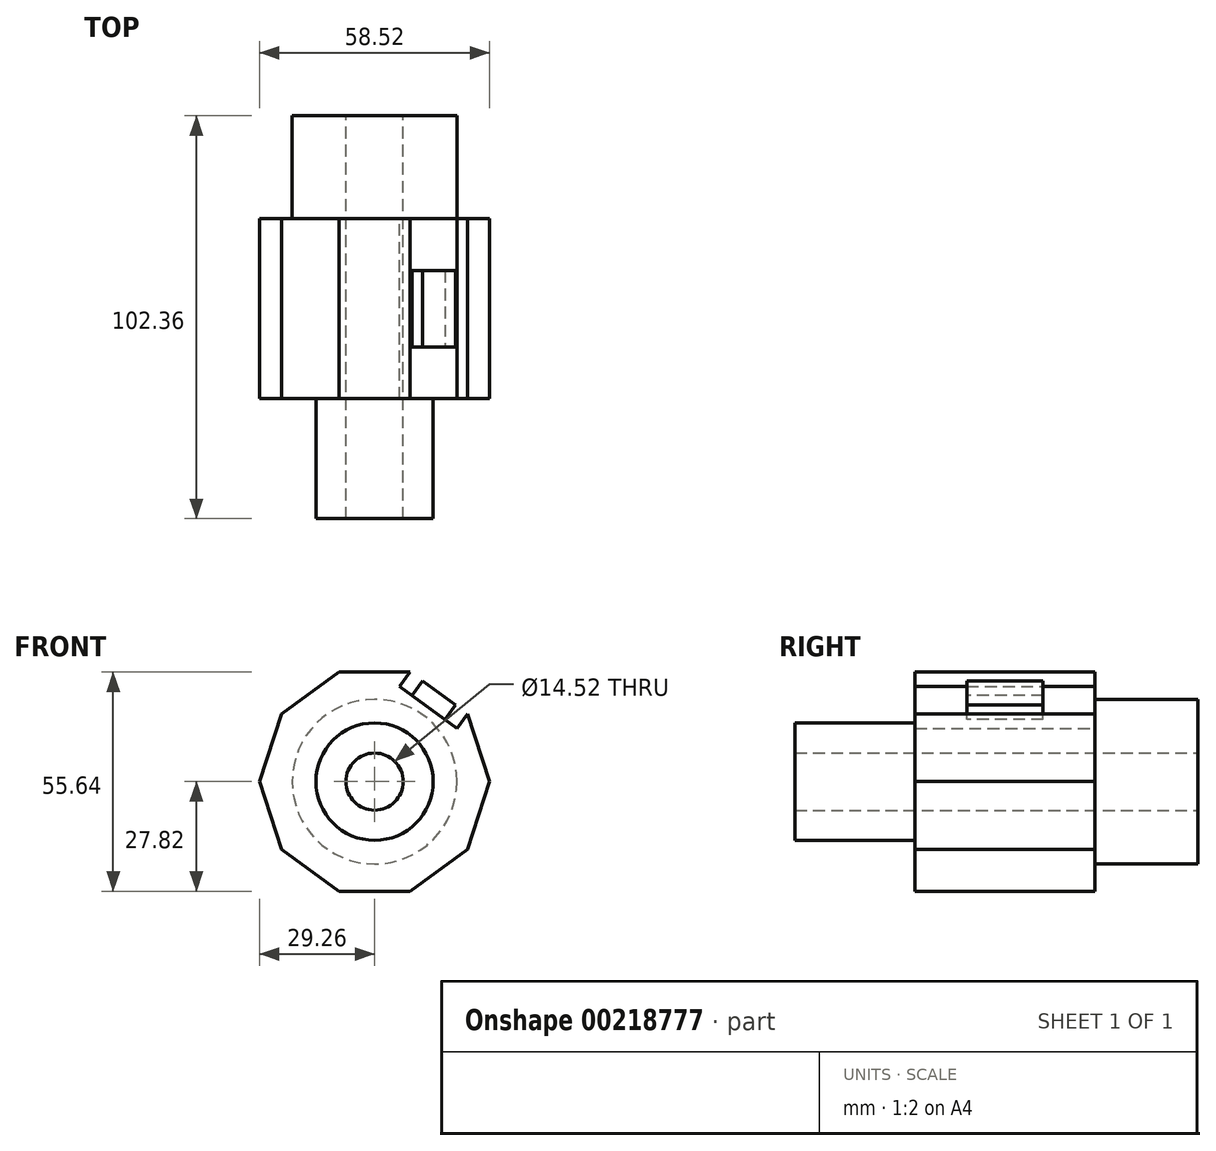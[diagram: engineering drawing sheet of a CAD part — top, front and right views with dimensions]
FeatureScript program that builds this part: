
annotation { "Feature Type Name" : "Feature", "Feature Type Description" : "" }
export const myFeature = defineFeature(function(context is Context, id is Id, definition is map)
    precondition{}
    {
        {
            var Q0;
            Q0=qCreatedBy(makeId("Front.planeOp"),FACE);
            var sketch = newSketch(context, id + "F0", { "sketchPlane" : qUnion([Q0])});
            skCircle(sketch, "E0.cCircle", {"center": v(0, 0) * mm, "radius": 27.82 * mm, "construction": true});
            skLineSegment(sketch, "E0.0", {"start": v(-9.04, 27.82) * mm, "end": v(9.04, 27.82) * mm});
            skLineSegment(sketch, "E0.1", {"start": v(9.04, 27.82) * mm, "end": v(23.67, 17.2) * mm});
            skLineSegment(sketch, "E0.2", {"start": v(23.67, 17.2) * mm, "end": v(29.26, 0) * mm});
            skLineSegment(sketch, "E0.3", {"start": v(29.26, 0) * mm, "end": v(23.67, -17.2) * mm});
            skLineSegment(sketch, "E0.4", {"start": v(23.67, -17.2) * mm, "end": v(9.04, -27.82) * mm});
            skLineSegment(sketch, "E0.5", {"start": v(9.04, -27.82) * mm, "end": v(-9.04, -27.82) * mm});
            skLineSegment(sketch, "E0.6", {"start": v(-9.04, -27.82) * mm, "end": v(-23.67, -17.2) * mm});
            skLineSegment(sketch, "E0.7", {"start": v(-23.67, -17.2) * mm, "end": v(-29.26, 0) * mm});
            skLineSegment(sketch, "E0.8", {"start": v(-29.26, 0) * mm, "end": v(-23.67, 17.2) * mm});
            skLineSegment(sketch, "E0.9", {"start": v(-23.67, 17.2) * mm, "end": v(-9.04, 27.82) * mm});
            skPoint(sketch, "E0.0.midPoint", {"position": v(0, 27.82) * mm});
            skSolve(sketch);
        }
        {
            var Q0;
            Q0=makeQuery(id+"F0.imprint","IMPRINT",FACE,{"disambiguationData":[TD([[makeQuery(id+"F0.imprint","IMPRINT",EDGE,{"derivedFrom":sQuery(id+"F0.wireOp",EDGE,"E0.0")}),-1.0]])]});
            extrude(context, id + "F1", {"entities" : qUnion([Q0]), "depth" : 76.2 * mm});
        }
        {
            var Q0;
            Q0=makeQuery(id+"F1.opExtrude","CAP_FACE",FACE,{"disambiguationData":[OSD([sQuery(id+"F0.wireOp",EDGE,"E0.0"),sQuery(id+"F0.wireOp",EDGE,"E0.1"),sQuery(id+"F0.wireOp",EDGE,"E0.2"),sQuery(id+"F0.wireOp",EDGE,"E0.3"),sQuery(id+"F0.wireOp",EDGE,"E0.4"),sQuery(id+"F0.wireOp",EDGE,"E0.5"),sQuery(id+"F0.wireOp",EDGE,"E0.6"),sQuery(id+"F0.wireOp",EDGE,"E0.7"),sQuery(id+"F0.wireOp",EDGE,"E0.8"),sQuery(id+"F0.wireOp",EDGE,"E0.9")])],"isStart":false});
            var sketch = newSketch(context, id + "F2", { "sketchPlane" : qUnion([Q0])});
            skCircle(sketch, "E1", {"center": v(0, 0) * mm, "radius": 14.9 * mm});
            skSolve(sketch);
        }
        {
            var Q0;
            Q0=makeQuery(id+"F2.imprint","IMPRINT",FACE,{"disambiguationData":[TD([[makeQuery(id+"F2.imprint","IMPRINT",EDGE,{"derivedFrom":sQuery(id+"F2.wireOp",EDGE,"E1")}),-1.0]])]});
            extrude(context, id + "F3", {"entities" : qUnion([Q0]), "operationType" : NewBodyOperationType.REMOVE, "oppositeDirection" : true, "depth" : 30.48 * mm});
        }
        {
            var Q0;
            Q0=qCreatedBy(makeId("Front.planeOp"),FACE);
            var sketch = newSketch(context, id + "F4", { "sketchPlane" : qUnion([Q0])});
            skCircle(sketch, "E2", {"center": v(0, 0) * mm, "radius": 20.93 * mm});
            skSolve(sketch);
        }
        {
            var Q0;
            Q0=makeQuery(id+"F4.imprint","IMPRINT",FACE,{"disambiguationData":[TD([[makeQuery(id+"F4.imprint","IMPRINT",EDGE,{"derivedFrom":sQuery(id+"F4.wireOp",EDGE,"E2")}),1.0]])]});
            extrude(context, id + "F5", {"entities" : qUnion([Q0]), "operationType" : NewBodyOperationType.ADD, "oppositeDirection" : true, "depth" : 26.16 * mm});
        }
        {
            var Q0;
            Q0=makeQuery(id+"F1.opExtrude","SWEPT_FACE",FACE,{"disambiguationData":[OSD([sQuery(id+"F0.wireOp",EDGE,"E0.1")])]});
            var sketch = newSketch(context, id + "F6", { "sketchPlane" : qUnion([Q0])});
            skLineSegment(sketch, "E3.bottom", {"start": v(5.2, -13.17) * mm, "end": v(-5.2, -13.17) * mm});
            skLineSegment(sketch, "E3.top", {"start": v(5.2, -32.55) * mm, "end": v(-5.2, -32.55) * mm});
            skLineSegment(sketch, "E3.left", {"start": v(5.2, -13.17) * mm, "end": v(5.2, -32.55) * mm});
            skLineSegment(sketch, "E3.right", {"start": v(-5.2, -13.17) * mm, "end": v(-5.2, -32.55) * mm});
            skPoint(sketch, "E3.middle", {"position": v(0, -22.86) * mm});
            skPoint(sketch, "E3.middle.positionSnap0", {"position": v(9.04, -22.86) * mm});
            skPoint(sketch, "E3.centerSnap0", {"position": v(9.04, -22.86) * mm});
            skSolve(sketch);
        }
        {
            var Q0;
            Q0=makeQuery(id+"F6.imprint","IMPRINT",FACE,{"disambiguationData":[TD([[makeQuery(id+"F6.imprint","IMPRINT",EDGE,{"derivedFrom":sQuery(id+"F6.wireOp",EDGE,"E3.bottom")}),-1.0]])]});
            extrude(context, id + "F7", {"entities" : qUnion([Q0]), "operationType" : NewBodyOperationType.REMOVE, "oppositeDirection" : true, "depth" : 4.57 * mm});
        }
        {
            var Q0;
            Q0=makeQuery(id+"F5.opExtrude","CAP_FACE",FACE,{"disambiguationData":[OSD([sQuery(id+"F4.wireOp",EDGE,"E2")])],"isStart":false});
            var sketch = newSketch(context, id + "F8", { "sketchPlane" : qUnion([Q0])});
            skCircle(sketch, "E4", {"center": v(0, 0) * mm, "radius": 7.26 * mm});
            skSolve(sketch);
        }
        {
            var Q0;
            Q0=makeQuery(id+"F8.imprint","IMPRINT",FACE,{"disambiguationData":[TD([[makeQuery(id+"F8.imprint","IMPRINT",EDGE,{"derivedFrom":sQuery(id+"F8.wireOp",EDGE,"E4")}),1.0]])]});
            extrude(context, id + "F9", {"entities" : qUnion([Q0]), "operationType" : NewBodyOperationType.REMOVE, "oppositeDirection" : true, "depth" : 111 * mm});
        }
    });
